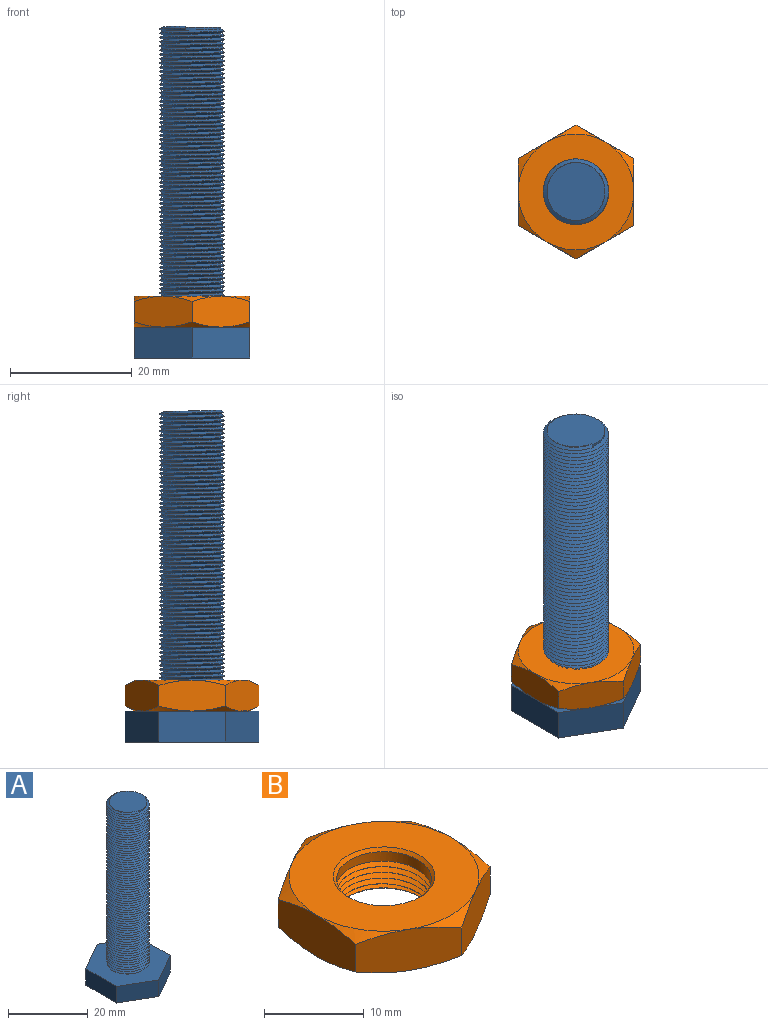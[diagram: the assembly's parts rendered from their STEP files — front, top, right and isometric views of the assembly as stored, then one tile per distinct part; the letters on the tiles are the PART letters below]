
ASSEMBLY  parts=2 mates=1
PART A: 138 faces, bbox 19.6x22.5x55.2 mm
  f0: plane 22x19.05mm, normal (0,0,-1), area 260.7mm2, adj f34,f35,f36,f37,f38,f39,f40,f41
  f1: cylinder r=4.76mm len=49.28mm, axis (0,0,-1), area 41.2mm2, adj f2,f4,f5,f6,f7,f8,f9,f10
  f2: plane 9.53x9.53mm, normal (0,0,1), area 71.3mm2, adj f1,f3
  f3: cylinder r=4.76mm len=7.56mm, axis (0,0,1), area 1.1mm2, adj f2,f27,f28
  f4: bspline ~12.37x10.71mm, area 119mm2, adj f1,f5,f7,f33
  f5: bspline ~12.37x10.71mm, area 108.7mm2, adj f1,f4,f6,f33
  f6: bspline ~12.37x10.71mm, area 108.9mm2, adj f1,f5,f7,f8
  f7: bspline ~12.37x10.71mm, area 108.9mm2, adj f1,f4,f6,f9
  f8: bspline ~12.37x10.71mm, area 108.9mm2, adj f1,f6,f9,f10
  f9: bspline ~12.37x10.71mm, area 108.9mm2, adj f1,f7,f8,f11
  f10: bspline ~12.37x10.71mm, area 108.9mm2, adj f1,f8,f11,f13
  f11: bspline ~12.37x10.71mm, area 108.9mm2, adj f1,f9,f10,f12
  f12: bspline ~12.37x10.71mm, area 93.3mm2, adj f1,f11,f13,f16
  f13: bspline ~12.37x10.71mm, area 93.3mm2, adj f1,f10,f12,f17
  f14: bspline ~12.37x10.71mm, area 124.4mm2, adj f1,f15,f16,f18
  f15: bspline ~12.37x10.71mm, area 124.4mm2, adj f1,f14,f17,f19
  f16: bspline ~12.37x10.71mm, area 108.8mm2, adj f1,f12,f14,f17
  f17: bspline ~12.37x10.71mm, area 108.8mm2, adj f1,f13,f15,f16
  f18: bspline ~12.37x10.71mm, area 93.3mm2, adj f1,f14,f19,f31
  f19: bspline ~12.37x10.71mm, area 93.3mm2, adj f1,f15,f18,f32
  f20: bspline ~12.37x10.71mm, area 124.4mm2, adj f1,f21,f22,f31
  f21: bspline ~12.37x10.71mm, area 124.4mm2, adj f1,f20,f23,f32
  f22: bspline ~12.37x10.71mm, area 93.3mm2, adj f1,f20,f23,f29
  f23: bspline ~12.37x10.71mm, area 93.3mm2, adj f1,f21,f22,f30
  f24: bspline ~12.37x10.71mm, area 124.3mm2, adj f1,f25,f28,f29
  f25: bspline ~12.37x10.71mm, area 124.4mm2, adj f1,f24,f26,f30
  f26: bspline ~12.37x10.71mm, area 108.9mm2, adj f1,f25,f27,f28
  f27: plane 0.69x0.58mm, normal (0.97,-0.22,0), area 0.2mm2, adj f1,f3,f26,f28
  f28: bspline ~12.37x10.71mm, area 108.9mm2, adj f1,f3,f24,f26,f27
  f29: bspline ~12.37x10.71mm, area 108.8mm2, adj f1,f22,f24,f30
  f30: bspline ~12.37x10.71mm, area 108.8mm2, adj f1,f23,f25,f29
  f31: bspline ~12.37x10.71mm, area 108.8mm2, adj f1,f18,f20,f32
  f32: bspline ~12.37x10.71mm, area 108.8mm2, adj f1,f19,f21,f31
  f33: plane 22.5x19.55mm, normal (0,0,1), area 234mm2, adj f1,f4,f5,f34,f35,f36,f37,f38
  f34: plane 11x5.08mm, normal (1,0,0), area 55.9mm2, adj f0,f33,f35,f39
  f35: plane 9.53x5.5mm, normal (0.5,0.87,0), area 55.9mm2, adj f0,f33,f34,f36
  f36: plane 9.53x5.5mm, normal (-0.5,0.87,0), area 55.9mm2, adj f0,f33,f35,f37
  f37: plane 11x5.08mm, normal (-1,0,0), area 55.9mm2, adj f0,f33,f36,f38
  f38: plane 9.53x5.5mm, normal (-0.5,-0.87,0), area 55.9mm2, adj f0,f33,f37,f39
  f39: plane 9.53x5.5mm, normal (0.5,-0.87,0), area 55.9mm2, adj f0,f33,f34,f38
  f40: plane 3.78x2.54mm, normal (1,0,0), area 9.6mm2, adj f0,f41,f43,f44
  f41: plane 2.54x0.8mm, normal (0,-1,0), area 2mm2, adj f0,f40,f42,f44
  f42: plane 3.78x2.54mm, normal (-1,0,0), area 9.6mm2, adj f0,f41,f43,f44
  f43: plane 2.54x0.8mm, normal (0,1,0), area 2mm2, adj f0,f40,f42,f44
  f44: plane 3.78x0.8mm, normal (0,0,-1), area 3mm2, adj f40,f41,f42,f43
  f45: plane 2.54x2.18mm, normal (0,-1,0), area 5.5mm2, adj f0,f46,f56,f57
  f46: plane 2.54x0.66mm, normal (-1,0,0), area 1.7mm2, adj f0,f45,f47,f57
  f47: plane 2.54x1.37mm, normal (0,1,0), area 3.5mm2, adj f0,f46,f48,f57
  f48: plane 2.54x0.97mm, normal (-1,0,0), area 2.5mm2, adj f0,f47,f49,f57
  f49: plane 2.54x1.28mm, normal (0,-1,0), area 3.2mm2, adj f0,f48,f50,f57
  f50: plane 2.54x0.66mm, normal (-1,0,0), area 1.7mm2, adj f0,f49,f51,f57
  f51: plane 2.54x1.28mm, normal (0,1,0), area 3.2mm2, adj f0,f50,f52,f57
  f52: plane 2.54x0.83mm, normal (-1,0,0), area 2.1mm2, adj f0,f51,f53,f57
  f53: plane 2.54x1.37mm, normal (0,-1,0), area 3.5mm2, adj f0,f52,f54,f57
  f54: plane 2.54x0.66mm, normal (-1,0,0), area 1.7mm2, adj f0,f53,f55,f57
  f55: plane 2.54x2.18mm, normal (0,1,0), area 5.5mm2, adj f0,f54,f56,f57
  f56: plane 3.78x2.54mm, normal (1,0,0), area 9.6mm2, adj f0,f45,f55,f57
  f57: plane 3.78x2.18mm, normal (0,0,-1), area 5.7mm2, adj f45,f46,f47,f48,f49,f50,f51,f52
  f58: extruded ~2.54x0.95mm, area 2.5mm2, adj f59,f71,f72,f136
  f59: extruded ~2.54x0.95mm, area 2.5mm2, adj f58,f60,f72,f136
  f60: extruded ~2.54x0.72mm, area 2.1mm2, adj f59,f61,f72,f136
  f61: extruded ~2.54x1.28mm, area 4.6mm2, adj f60,f62,f72,f136
  f62: extruded ~2.54x1.27mm, area 4.6mm2, adj f61,f71,f72,f136
  f63: extruded ~2.54x1.44mm, area 3.9mm2, adj f0,f64,f70,f72
  f64: extruded ~2.54x1.44mm, area 3.9mm2, adj f0,f63,f65,f72
  f65: extruded ~2.54x1.33mm, area 3.7mm2, adj f0,f64,f66,f72
  f66: extruded ~2.54x1.34mm, area 3.7mm2, adj f0,f65,f67,f72
  f67: extruded ~2.54x1.44mm, area 3.9mm2, adj f0,f66,f68,f72
  f68: extruded ~2.54x1.45mm, area 4mm2, adj f0,f67,f69,f72
  f69: extruded ~2.54x1.33mm, area 3.7mm2, adj f0,f68,f70,f72
  f70: extruded ~2.54x1.33mm, area 3.7mm2, adj f0,f63,f69,f72
  f71: extruded ~2.54x0.72mm, area 2.1mm2, adj f58,f62,f72,f136
  f72: plane 3.89x3.6mm, normal (0,0,-1), area 7.5mm2, adj f58,f59,f60,f61,f62,f63,f64,f65
  f73: extruded ~2.54x1.38mm, area 3.7mm2, adj f74,f84,f85,f137
  f74: plane 2.54x0.98mm, normal (0,1,0), area 2.5mm2, adj f73,f75,f85,f137
  f75: extruded ~2.54x1.64mm, area 4.3mm2, adj f74,f84,f85,f137
  f76: plane 2.54x0.9mm, normal (0.96,-0.29,0), area 2.4mm2, adj f0,f77,f83,f85
  f77: plane 2.54x0.86mm, normal (0,-1,0), area 2.2mm2, adj f0,f76,f78,f85
  f78: plane 3.79x2.54mm, normal (-0.94,0.33,0), area 10.2mm2, adj f0,f77,f79,f85
  f79: plane 2.54x0.98mm, normal (0,1,0), area 2.5mm2, adj f0,f78,f80,f85
  f80: plane 3.79x2.54mm, normal (0.94,0.33,0), area 10.2mm2, adj f0,f79,f81,f85
  f81: plane 2.54x0.86mm, normal (0,-1,0), area 2.2mm2, adj f0,f80,f82,f85
  f82: plane 2.54x0.9mm, normal (-0.96,-0.29,0), area 2.4mm2, adj f0,f81,f83,f85
  f83: plane 2.54x1.38mm, normal (0,-1,0), area 3.5mm2, adj f0,f76,f82,f85
  f84: extruded ~2.54x0.25mm, area 0.7mm2, adj f73,f75,f85,f137
  f85: plane 3.79x3.65mm, normal (0,0,-1), area 6.5mm2, adj f73,f74,f75,f76,f77,f78,f79,f80
  f86: plane 2.54x0.8mm, normal (0,-1,0), area 2mm2, adj f0,f87,f93,f94
  f87: plane 3.11x2.54mm, normal (-1,0,0), area 7.9mm2, adj f0,f86,f88,f94
  f88: plane 2.54x1.03mm, normal (0,-1,0), area 2.6mm2, adj f0,f87,f89,f94
  f89: plane 2.54x0.67mm, normal (-1,0,0), area 1.7mm2, adj f0,f88,f90,f94
  f90: plane 2.85x2.54mm, normal (0,1,0), area 7.2mm2, adj f0,f89,f91,f94
  f91: plane 2.54x0.67mm, normal (1,0,0), area 1.7mm2, adj f0,f90,f92,f94
  f92: plane 2.54x1.03mm, normal (0,-1,0), area 2.6mm2, adj f0,f91,f93,f94
  f93: plane 3.11x2.54mm, normal (1,0,0), area 7.9mm2, adj f0,f86,f92,f94
  f94: plane 3.78x2.85mm, normal (0,0,-1), area 4.4mm2, adj f86,f87,f88,f89,f90,f91,f92,f93
  f95: plane 2.54x0.81mm, normal (0,1,0), area 2.1mm2, adj f0,f96,f104,f105
  f96: plane 2.54x2.25mm, normal (0.95,0.3,0), area 6mm2, adj f0,f95,f97,f105
  f97: extruded ~2.54x0.83mm, area 2.2mm2, adj f0,f96,f98,f105
  f98: extruded ~2.54x0.37mm, area 1mm2, adj f0,f97,f99,f105
  f99: extruded ~2.54x0.46mm, area 1.2mm2, adj f0,f98,f100,f105
  f100: plane 2.54x2.25mm, normal (-0.95,0.3,0), area 6mm2, adj f0,f99,f101,f105
  f101: plane 2.54x0.81mm, normal (0,1,0), area 2.1mm2, adj f0,f100,f102,f105
  f102: plane 3.78x2.54mm, normal (0.95,-0.32,0), area 10.1mm2, adj f0,f101,f103,f105
  f103: plane 2.54x0.87mm, normal (0,-1,0), area 2.2mm2, adj f0,f102,f104,f105
  f104: plane 3.78x2.54mm, normal (-0.95,-0.32,0), area 10.1mm2, adj f0,f95,f103,f105
  f105: plane 3.78x3.44mm, normal (0,0,-1), area 5.5mm2, adj f95,f96,f97,f98,f99,f100,f101,f102
  f106: plane 2.54x1.02mm, normal (0,-1,0), area 2.6mm2, adj f0,f107,f119,f120
  f107: plane 3.78x2.54mm, normal (-1,0,0), area 9.6mm2, adj f0,f106,f108,f120
  f108: plane 2.54x0.72mm, normal (0,1,0), area 1.8mm2, adj f0,f107,f109,f120
  f109: plane 2.54x1.79mm, normal (1,0,0), area 4.5mm2, adj f0,f108,f110,f120
  f110: extruded ~2.54x1.04mm, area 2.6mm2, adj f0,f109,f111,f120
  f111: plane 2.54x0.02mm, normal (0,1,0), area 0mm2, adj f0,f110,f112,f120
  f112: plane 2.83x2.54mm, normal (-0.87,0.5,0), area 8.3mm2, adj f0,f111,f113,f120
  f113: plane 2.54x1.01mm, normal (0,1,0), area 2.6mm2, adj f0,f112,f114,f120
  f114: plane 3.78x2.54mm, normal (1,0,0), area 9.6mm2, adj f0,f113,f115,f120
  f115: plane 2.54x0.72mm, normal (0,-1,0), area 1.8mm2, adj f0,f114,f116,f120
  f116: plane 2.54x1.78mm, normal (-1,0,0), area 4.5mm2, adj f0,f115,f117,f120
  f117: extruded ~2.54x1.08mm, area 2.7mm2, adj f0,f116,f118,f120
  f118: plane 2.54x0.02mm, normal (0,-1,0), area 0.1mm2, adj f0,f117,f119,f120
  f119: plane 2.86x2.54mm, normal (0.87,-0.5,0), area 8.4mm2, adj f0,f106,f118,f120
  f120: plane 3.78x3.35mm, normal (0,0,-1), area 8.1mm2, adj f106,f107,f108,f109,f110,f111,f112,f113
  f121: plane 2.54x1.02mm, normal (0,-1,0), area 2.6mm2, adj f0,f122,f134,f135
  f122: plane 3.78x2.54mm, normal (-1,0,0), area 9.6mm2, adj f0,f121,f123,f135
  f123: plane 2.54x0.72mm, normal (0,1,0), area 1.8mm2, adj f0,f122,f124,f135
  f124: plane 2.54x1.79mm, normal (1,0,0), area 4.5mm2, adj f0,f123,f125,f135
  f125: extruded ~2.54x1.04mm, area 2.6mm2, adj f0,f124,f126,f135
  f126: plane 2.54x0.02mm, normal (0,1,0), area 0mm2, adj f0,f125,f127,f135
  f127: plane 2.83x2.54mm, normal (-0.87,0.5,0), area 8.3mm2, adj f0,f126,f128,f135
  f128: plane 2.54x1.01mm, normal (0,1,0), area 2.6mm2, adj f0,f127,f129,f135
  f129: plane 3.78x2.54mm, normal (1,0,0), area 9.6mm2, adj f0,f128,f130,f135
  f130: plane 2.54x0.72mm, normal (0,-1,0), area 1.8mm2, adj f0,f129,f131,f135
  f131: plane 2.54x1.78mm, normal (-1,0,0), area 4.5mm2, adj f0,f130,f132,f135
  f132: extruded ~2.54x1.08mm, area 2.7mm2, adj f0,f131,f133,f135
  f133: plane 2.54x0.02mm, normal (0,-1,0), area 0.1mm2, adj f0,f132,f134,f135
  f134: plane 2.86x2.54mm, normal (0.87,-0.5,0), area 8.4mm2, adj f0,f121,f133,f135
  f135: plane 3.78x3.35mm, normal (0,0,-1), area 8.1mm2, adj f121,f122,f123,f124,f125,f126,f127,f128
  f136: plane 2.55x1.92mm, normal (0,0,-1), area 4.1mm2, adj f58,f59,f60,f61,f62,f71
  f137: plane 1.64x0.98mm, normal (0,0,-1), area 0.8mm2, adj f73,f74,f75,f84
PART B: 31 faces, bbox 22.9x22.9x6.4 mm
  f0: plane 10.43x6.4mm, normal (0.5,-0.87,0), area 49.5mm2, adj f1,f5,f18,f19,f20,f21
  f1: plane 11.91x5.99mm, normal (1,0,0), area 49.5mm2, adj f0,f2,f14,f19,f20,f25
  f2: plane 10.43x6.4mm, normal (0.5,0.87,0), area 49.5mm2, adj f1,f3,f14,f15,f24,f25
  f3: plane 10.43x6.4mm, normal (-0.5,0.87,0), area 49.5mm2, adj f2,f4,f15,f16,f23,f24
  f4: plane 11.91x5.99mm, normal (-1,0,0), area 49.5mm2, adj f3,f5,f16,f17,f22,f23
  f5: plane 10.43x6.4mm, normal (-0.5,-0.87,0), area 49.5mm2, adj f0,f4,f17,f18,f21,f22
  f6: plane 19.21x19.21mm, normal (0,0,-1), area 201.5mm2, adj f20,f21,f22,f23,f24,f25,f27,f28
  f7: plane 19.05x19.05mm, normal (0,0,1), area 203.3mm2, adj f14,f15,f16,f17,f18,f19,f26
  f8: cylinder r=4.76mm len=9.53mm, axis (0,0,-1), area 32.8mm2, adj f9,f26,f28,f29,f30
  f9: cylinder r=4.76mm len=9.53mm, axis (0,0,-1), area 0.4mm2, adj f8,f10,f28,f29
  f10: cylinder r=4.76mm len=9.53mm, axis (0,0,-1), area 0.4mm2, adj f9,f11,f28,f29
  f11: cylinder r=4.76mm len=9.53mm, axis (0,0,-1), area 0.4mm2, adj f10,f12,f28,f29
  f12: cylinder r=4.76mm len=9.53mm, axis (0,0,-1), area 0.4mm2, adj f11,f13,f28,f29
  f13: cylinder r=4.76mm len=0.64mm, axis (0,0,-1), area 0mm2, adj f12,f27,f29
  f14: cone r=9.53mm half-angle=60deg, axis (0,0,-1), area 8.9mm2, adj f1,f2,f7
  f15: cone r=9.53mm half-angle=60deg, axis (0,0,-1), area 8.9mm2, adj f2,f3,f7
  f16: cone r=9.53mm half-angle=60deg, axis (0,0,-1), area 8.9mm2, adj f3,f4,f7
  f17: cone r=9.53mm half-angle=60deg, axis (0,0,-1), area 8.9mm2, adj f4,f5,f7
  f18: cone r=9.53mm half-angle=60deg, axis (0,0,-1), area 8.9mm2, adj f0,f5,f7
  f19: cone r=9.53mm half-angle=60deg, axis (0,0,-1), area 8.9mm2, adj f0,f1,f7
  f20: cone r=9.53mm half-angle=60deg, axis (0,0,1), area 8.9mm2, adj f0,f1,f6
  f21: cone r=9.53mm half-angle=60deg, axis (0,0,1), area 8.9mm2, adj f0,f5,f6
  f22: cone r=9.53mm half-angle=60deg, axis (0,0,1), area 8.9mm2, adj f4,f5,f6
  f23: cone r=9.53mm half-angle=60deg, axis (0,0,1), area 8.9mm2, adj f3,f4,f6
  f24: cone r=9.53mm half-angle=60deg, axis (0,0,1), area 8.9mm2, adj f2,f3,f6
  f25: cone r=9.53mm half-angle=60deg, axis (0,0,1), area 8.9mm2, adj f1,f2,f6
  f26: cone r=4.76mm half-angle=45deg, axis (0,0,1), area 14.8mm2, adj f7,f8
  f27: cone r=5.1mm half-angle=45deg, axis (0,0,-1), area 4.5mm2, adj f6,f13,f28,f29
  f28: bspline ~12.37x10.71mm, area 116.1mm2, adj f6,f8,f9,f10,f11,f12,f27,f29
  f29: bspline ~12.37x10.71mm, area 105.7mm2, adj f6,f8,f9,f10,f11,f12,f13,f27
  f30: plane 0.69x0.58mm, normal (-0.97,0.22,0), area 0.2mm2, adj f8,f28,f29
PLACE A at identity fixed
PLACE B at identity
MATE cylindrical A.f1 <-> B.f8  axis (0,0,1) through (0,0,0)mm
